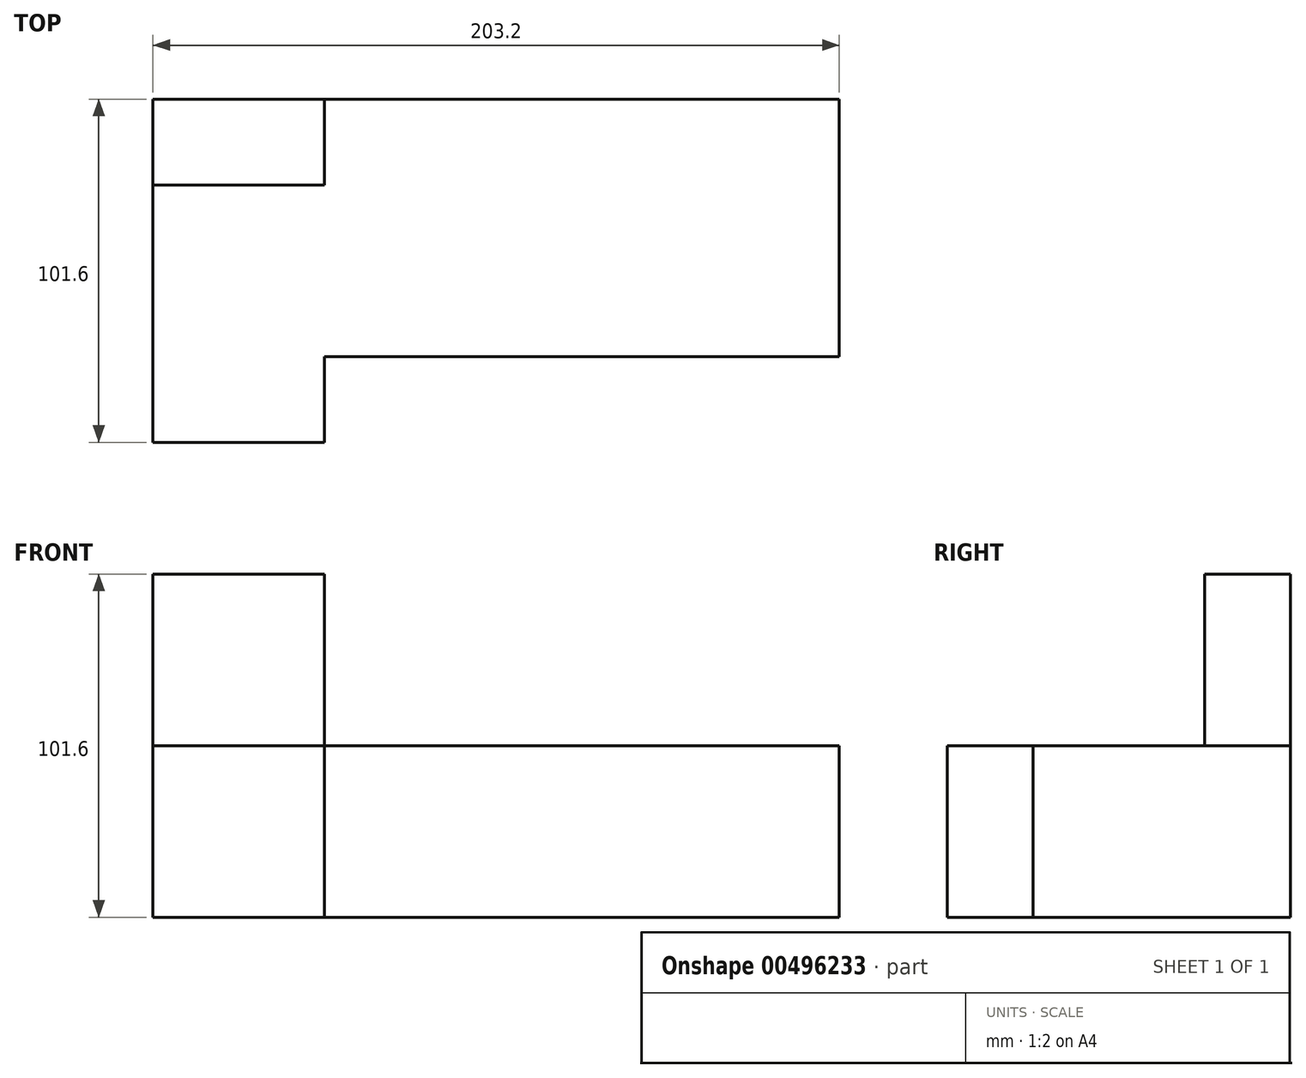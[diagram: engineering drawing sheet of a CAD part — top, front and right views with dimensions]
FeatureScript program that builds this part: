
annotation { "Feature Type Name" : "Feature", "Feature Type Description" : "" }
export const myFeature = defineFeature(function(context is Context, id is Id, definition is map)
    precondition{}
    {
        {
            var Q0;
            Q0=qCreatedBy(makeId("Front.planeOp"),FACE);
            var sketch = newSketch(context, id + "F0", { "sketchPlane" : qUnion([Q0])});
            skLineSegment(sketch, "E0.bottom", {"start": v(0, 0) * mm, "end": v(76.2, 0) * mm});
            skLineSegment(sketch, "E0.top", {"start": v(0, 50.8) * mm, "end": v(76.2, 50.8) * mm});
            skLineSegment(sketch, "E0.left", {"start": v(0, 0) * mm, "end": v(0, 50.8) * mm});
            skLineSegment(sketch, "E0.right", {"start": v(76.2, 0) * mm, "end": v(76.2, 50.8) * mm});
            skSolve(sketch);
        }
        {
            var Q0;
            Q0 = qSketchRegion(id + "F0", true);
            extrude(context, id + "F1", {"entities" : qUnion([Q0]), "depth" : 203.2 * mm});
        }
        {
            var Q0;
            Q0=qCreatedBy(makeId("Top.planeOp"),FACE);
            var sketch = newSketch(context, id + "F2", { "sketchPlane" : qUnion([Q0])});
            skLineSegment(sketch, "E1.bottom", {"start": v(0, 0) * mm, "end": v(-25.4, 0) * mm});
            skLineSegment(sketch, "E1.top", {"start": v(0, -50.8) * mm, "end": v(-25.4, -50.8) * mm});
            skLineSegment(sketch, "E1.left", {"start": v(0, 0) * mm, "end": v(0, -50.8) * mm});
            skLineSegment(sketch, "E1.right", {"start": v(-25.4, 0) * mm, "end": v(-25.4, -50.8) * mm});
            skSolve(sketch);
        }
        {
            var Q0;
            Q0 = qSketchRegion(id + "F2", true);
            extrude(context, id + "F3", {"entities" : qUnion([Q0]), "operationType" : NewBodyOperationType.ADD, "depth" : 50.8 * mm});
        }
        {
            var Q0;
            Q0=makeQuery(id+"F3.boolean.opBoolean","MERGE",FACE,{"derivedFrom":[makeQuery(id+"F1.opExtrude","SWEPT_FACE",FACE,{"disambiguationData":[OSD([sQuery(id+"F0.wireOp",EDGE,"E0.top")])]}),makeQuery(id+"F3.opExtrude","CAP_FACE",FACE,{"disambiguationData":[OSD([sQuery(id+"F2.wireOp",EDGE,"E1.bottom"),sQuery(id+"F2.wireOp",EDGE,"E1.top"),sQuery(id+"F2.wireOp",EDGE,"E1.left"),sQuery(id+"F2.wireOp",EDGE,"E1.right")])],"isStart":false})]});
            var sketch = newSketch(context, id + "F4", { "sketchPlane" : qUnion([Q0])});
            skLineSegment(sketch, "E2", {"start": v(76.2, 0) * mm, "end": v(50.8, 0) * mm});
            skLineSegment(sketch, "E3", {"start": v(50.8, 0) * mm, "end": v(50.8, -50.8) * mm});
            skLineSegment(sketch, "E4", {"start": v(50.8, -50.8) * mm, "end": v(76.2, -50.8) * mm});
            skSolve(sketch);
        }
        {
            var Q0;
            {var subQ0=sQuery(id+"F4.wireOp",EDGE,"E2");Q0=makeQuery(id+"F4.imprint","IMPRINT",FACE,{"disambiguationData":[TD([[makeQuery(id+"F4.imprint","IMPRINT",EDGE,{"derivedFrom":subQ0}),-1.0]])]});}
            extrude(context, id + "F5", {"entities" : qUnion([Q0]), "operationType" : NewBodyOperationType.ADD, "depth" : 50.8 * mm});
        }
        {
            var Q0;
            Q0=makeQuery(id+"F1.opExtrude","SWEPT_BODY",BODY,{"disambiguationData":[OSD([sQuery(id+"F0.wireOp",EDGE,"E0.bottom"),sQuery(id+"F0.wireOp",EDGE,"E0.top"),sQuery(id+"F0.wireOp",EDGE,"E0.left"),sQuery(id+"F0.wireOp",EDGE,"E0.right")])]});
            var Q1;
            Q1=makeQuery(id+"F5.opExtrude","SWEPT_EDGE",EDGE,{"disambiguationData":[OSD([sQuery(id+"F4.wireOp",EDGE,"E3"),sQuery(id+"F4.wireOp",EDGE,"E4")])]});
            transform(context, id + "F6", {"entities" : qUnion([Q0]), "transformType" : TransformType.ROTATION, "transformAxis" : qUnion([Q1]), "angle" : 90 * degree, "makeCopy" : false});
        }
        {
            var Q0;
            Q0=makeQuery(id+"F1.opExtrude","SWEPT_BODY",BODY,{"disambiguationData":[OSD([sQuery(id+"F0.wireOp",EDGE,"E0.bottom"),sQuery(id+"F0.wireOp",EDGE,"E0.top"),sQuery(id+"F0.wireOp",EDGE,"E0.left"),sQuery(id+"F0.wireOp",EDGE,"E0.right")])]});
            var Q1;
            {var subQ0=sQuery(id+"F0.wireOp",EDGE,"E0.right");Q1=makeQuery(id+"F5.boolean.opBoolean","MERGE",EDGE,{"derivedFrom":[makeQuery(id+"F1.opExtrude","CAP_EDGE",EDGE,{"disambiguationData":[OSD([subQ0])],"isStart":true}),makeQuery(id+"F5.opExtrude","SWEPT_EDGE",EDGE,{"disambiguationData":[OSD([sQuery(id+"F0.wireOp",EDGE,"E0.top"),subQ0,sQuery(id+"F4.wireOp",EDGE,"E2")])]})]});}
            transform(context, id + "F7", {"entities" : qUnion([Q0]), "transformType" : TransformType.ROTATION, "transformAxis" : qUnion([Q1]), "angle" : 180 * degree, "makeCopy" : false});
        }
    });
